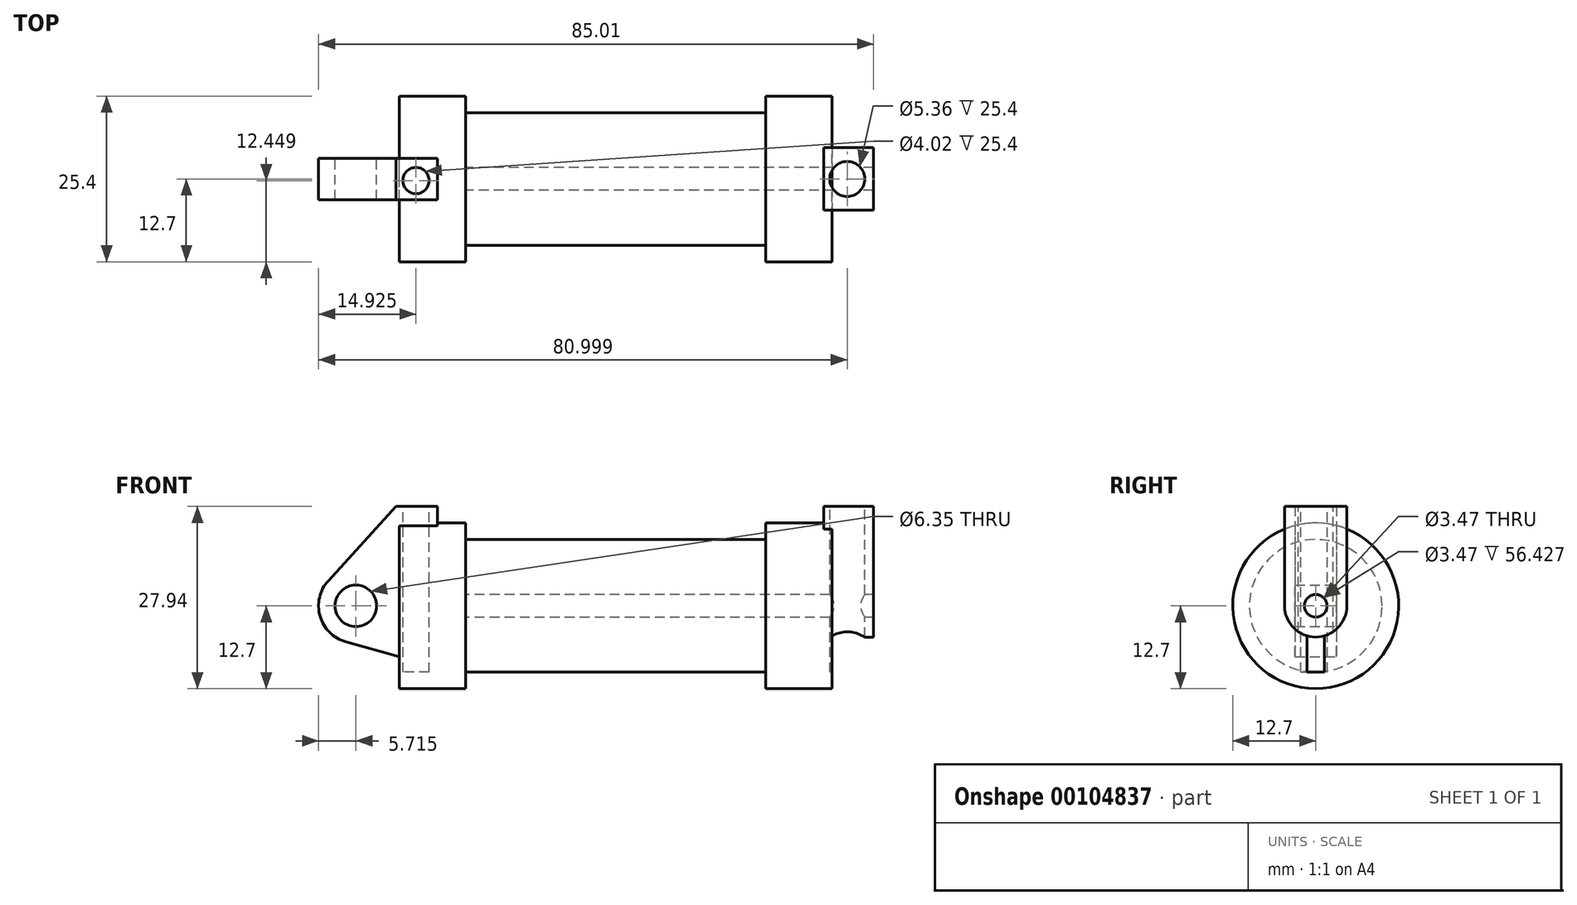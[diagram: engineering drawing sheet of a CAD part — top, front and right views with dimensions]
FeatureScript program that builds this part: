
annotation { "Feature Type Name" : "Feature", "Feature Type Description" : "" }
export const myFeature = defineFeature(function(context is Context, id is Id, definition is map)
    precondition{}
    {
        {
            var Q0;
            Q0=qCreatedBy(makeId("Front.planeOp"),FACE);
            var sketch = newSketch(context, id + "F0", { "sketchPlane" : qUnion([Q0])});
            skLineSegment(sketch, "E0", {"start": v(0, 0) * mm, "end": v(0, 12.7) * mm});
            skLineSegment(sketch, "E1", {"start": v(0, 12.7) * mm, "end": v(10.16, 12.7) * mm});
            skLineSegment(sketch, "E2", {"start": v(10.16, 12.7) * mm, "end": v(10.16, 10.16) * mm});
            skLineSegment(sketch, "E3", {"start": v(10.16, 10.16) * mm, "end": v(56.13, 10.16) * mm});
            skLineSegment(sketch, "E4", {"start": v(56.13, 10.16) * mm, "end": v(56.13, 12.7) * mm});
            skLineSegment(sketch, "E5", {"start": v(56.13, 12.7) * mm, "end": v(66.3, 12.7) * mm});
            skLineSegment(sketch, "E6", {"start": v(66.3, 12.7) * mm, "end": v(66.3, 0) * mm});
            skLineSegment(sketch, "E7", {"start": v(66.3, 0) * mm, "end": v(0, 0) * mm});
            skLineSegment(sketch, "E8", {"start": v(5.84, 15.24) * mm, "end": v(-0.5, 15.24) * mm});
            skLineSegment(sketch, "E9", {"start": v(-0.5, 15.24) * mm, "end": v(-10.88, 3.85) * mm});
            skLineSegment(sketch, "E10", {"start": v(0, 0) * mm, "end": v(-6.65, 0) * mm});
            skCircle(sketch, "E11", {"center": v(-6.65, 0) * mm, "radius": 5.72 * mm});
            skCircle(sketch, "E12", {"center": v(-6.65, 0) * mm, "radius": 3.18 * mm});
            skLineSegment(sketch, "E13", {"start": v(5.84, 15.24) * mm, "end": v(5.84, -9.4) * mm});
            skLineSegment(sketch, "E14", {"start": v(5.84, -9.4) * mm, "end": v(-8.18, -5.5) * mm});
            skSolve(sketch);
        }
        {
            var Q0;
            {var subQ0=sQuery(id+"F0.wireOp",EDGE,"E2");Q0=makeQuery(id+"F0.imprint","IMPRINT",FACE,{"disambiguationData":[TD([[makeQuery(id+"F0.imprint","IMPRINT",EDGE,{"derivedFrom":subQ0}),-1.0]])]});}
            var Q1;
            {var subQ0=sQuery(id+"F0.wireOp",EDGE,"E0");Q1=makeQuery(id+"F0.imprint","IMPRINT",FACE,{"disambiguationData":[TD([[makeQuery(id+"F0.imprint","IMPRINT",EDGE,{"derivedFrom":subQ0}),-1.0]])]});}
            var Q2;
            Q2=sQuery(id+"F0.wireOp",EDGE,"E7");
            revolve(context, id + "F1", {"entities" : qUnion([Q0, Q1]), "axis" : qUnion([Q2]), "revolveType" : RevolveType.FULL});
        }
        {
            var Q0;
            {var subQ0=sQuery(id+"F0.wireOp",EDGE,"E0");Q0=makeQuery(id+"F0.imprint","IMPRINT",FACE,{"disambiguationData":[TD([[makeQuery(id+"F0.imprint","IMPRINT",EDGE,{"derivedFrom":subQ0}),-1.0]])]});}
            var Q1;
            {var subQ3=sQuery(id+"F0.wireOp",EDGE,"E0");Q1=makeQuery(id+"F0.imprint","IMPRINT",FACE,{"disambiguationData":[TD([[makeQuery(id+"F0.imprint","IMPRINT",EDGE,{"derivedFrom":subQ3}),1.0]])]});}
            var Q2;
            {var subQ0=sQuery(id+"F0.wireOp",EDGE,"E14");Q2=makeQuery(id+"F0.imprint","IMPRINT",FACE,{"disambiguationData":[TD([[makeQuery(id+"F0.imprint","IMPRINT",EDGE,{"derivedFrom":subQ0}),-1.0]])]});}
            var Q3;
            {var subQ4=sQuery(id+"F0.wireOp",EDGE,"E12");Q3=makeQuery(id+"F0.imprint","IMPRINT",FACE,{"disambiguationData":[TD([[makeQuery(id+"F0.imprint","IMPRINT",EDGE,{"derivedFrom":subQ4}),-1.0]])]});}
            var Q4;
            {var subQ3=sQuery(id+"F0.wireOp",EDGE,"E0");Q4=makeQuery(id+"F0.imprint","IMPRINT",FACE,{"disambiguationData":[TD([[makeQuery(id+"F0.imprint","IMPRINT",EDGE,{"derivedFrom":subQ3}),1.0]])]});}
            var Q5;
            {var subQ0=sQuery(id+"F0.wireOp",EDGE,"E14");Q5=makeQuery(id+"F0.imprint","IMPRINT",FACE,{"disambiguationData":[TD([[makeQuery(id+"F0.imprint","IMPRINT",EDGE,{"derivedFrom":subQ0}),-1.0]])]});}
            var Q6;
            {var subQ4=sQuery(id+"F0.wireOp",EDGE,"E12");Q6=makeQuery(id+"F0.imprint","IMPRINT",FACE,{"disambiguationData":[TD([[makeQuery(id+"F0.imprint","IMPRINT",EDGE,{"derivedFrom":subQ4}),-1.0]])]});}
            extrude(context, id + "F2", {"entities" : qUnion([Q0, Q1, Q2, Q3, Q4, Q5, Q6]), "operationType" : NewBodyOperationType.ADD, "endBound" : BoundingType.SYMMETRIC, "depth" : 6.35 * mm});
        }
        {
            var Q0;
            {var subQ0=sQuery(id+"F0.wireOp",EDGE,"E6");Q0=makeQuery(id+"F2.boolean.opBoolean","MERGE",FACE,{"derivedFrom":[makeQuery(id+"F1.opRevolve","SWEPT_FACE",FACE,{"disambiguationData":[OSD([subQ0])]}),makeQuery(id+"F2.opExtrude","SWEPT_FACE",FACE,{"disambiguationData":[OSD([subQ0])]})]});}
            var sketch = newSketch(context, id + "F3", { "sketchPlane" : qUnion([Q0])});
            skCircle(sketch, "E15", {"center": v(0, 0) * mm, "radius": 1.73 * mm});
            skCircle(sketch, "E16", {"center": v(0, 0) * mm, "radius": 4.78 * mm});
            skLineSegment(sketch, "E17", {"start": v(-4.78, 0) * mm, "end": v(-4.78, 15.24) * mm});
            skLineSegment(sketch, "E18", {"start": v(4.78, 0) * mm, "end": v(4.78, 15.24) * mm});
            skLineSegment(sketch, "E19", {"start": v(-4.78, 15.24) * mm, "end": v(4.78, 15.24) * mm});
            skSolve(sketch);
        }
        {
            var Q0;
            Q0 = qSketchRegion(id + "F3", true);
            extrude(context, id + "F4", {"entities" : qUnion([Q0]), "operationType" : NewBodyOperationType.ADD, "depth" : 6.35 * mm, "hasSecondDirection" : true, "secondDirectionOppositeDirection" : true, "secondDirectionDepth" : 1.27 * mm});
        }
        {
            var Q0;
            Q0=makeQuery(id+"F4.boolean.opBoolean","SPLIT",FACE,{"disambiguationData":[TD([makeQuery(id+"F4.opExtrude","SWEPT_FACE",FACE,{"disambiguationData":[OSD([sQuery(id+"F3.wireOp",EDGE,"E15")])]})])],"derivedFrom":makeQuery(id+"F1.opRevolve","SWEPT_FACE",FACE,{"disambiguationData":[OSD([sQuery(id+"F0.wireOp",EDGE,"E6")])]})});
            var Q1;
            Q1=makeQuery(id+"F1.opRevolve","SWEPT_FACE",FACE,{"disambiguationData":[OSD([sQuery(id+"F0.wireOp",EDGE,"E2")])]});
            extrude(context, id + "F5", {"entities" : qUnion([Q0]), "operationType" : NewBodyOperationType.REMOVE, "endBound" : BoundingType.UP_TO_SURFACE, "oppositeDirection" : true, "endBoundEntityFace" : qUnion([Q1]), "depth" : 25.4 * mm});
        }
        {
            var Q0;
            Q0=makeQuery(id+"F4.opExtrude","SWEPT_FACE",FACE,{"disambiguationData":[OSD([sQuery(id+"F3.wireOp",EDGE,"E19")])]});
            var sketch = newSketch(context, id + "F6", { "sketchPlane" : qUnion([Q0])});
            skCircle(sketch, "E20", {"center": v(68.63, 0) * mm, "radius": 2.68 * mm});
            skPoint(sketch, "E20.centerSnap0", {"position": v(65.02, 0) * mm});
            skCircle(sketch, "E21", {"center": v(2.5, 0.15) * mm, "radius": 2.18 * mm});
            skSolve(sketch);
        }
        {
            var Q0;
            Q0=makeQuery(id+"F6.imprint","IMPRINT",FACE,{"disambiguationData":[TD([[makeQuery(id+"F6.imprint","IMPRINT",EDGE,{"derivedFrom":sQuery(id+"F6.wireOp",EDGE,"E20")}),1.0]])]});
            extrude(context, id + "F7", {"entities" : qUnion([Q0]), "operationType" : NewBodyOperationType.REMOVE, "oppositeDirection" : true, "depth" : 25.4 * mm});
        }
        {
            var Q0;
            Q0=makeQuery(id+"F2.opExtrude","SWEPT_FACE",FACE,{"disambiguationData":[OSD([sQuery(id+"F0.wireOp",EDGE,"E8")])]});
            var sketch = newSketch(context, id + "F8", { "sketchPlane" : qUnion([Q0])});
            skCircle(sketch, "E22", {"center": v(2.56, -0.25) * mm, "radius": 2 * mm});
            skSolve(sketch);
        }
        {
            var Q0;
            Q0=makeQuery(id+"F8.imprint","IMPRINT",FACE,{"disambiguationData":[TD([[makeQuery(id+"F8.imprint","IMPRINT",EDGE,{"derivedFrom":sQuery(id+"F8.wireOp",EDGE,"E22")}),1.0]])]});
            extrude(context, id + "F9", {"entities" : qUnion([Q0]), "operationType" : NewBodyOperationType.REMOVE, "oppositeDirection" : true, "depth" : 25.4 * mm});
        }
    });
